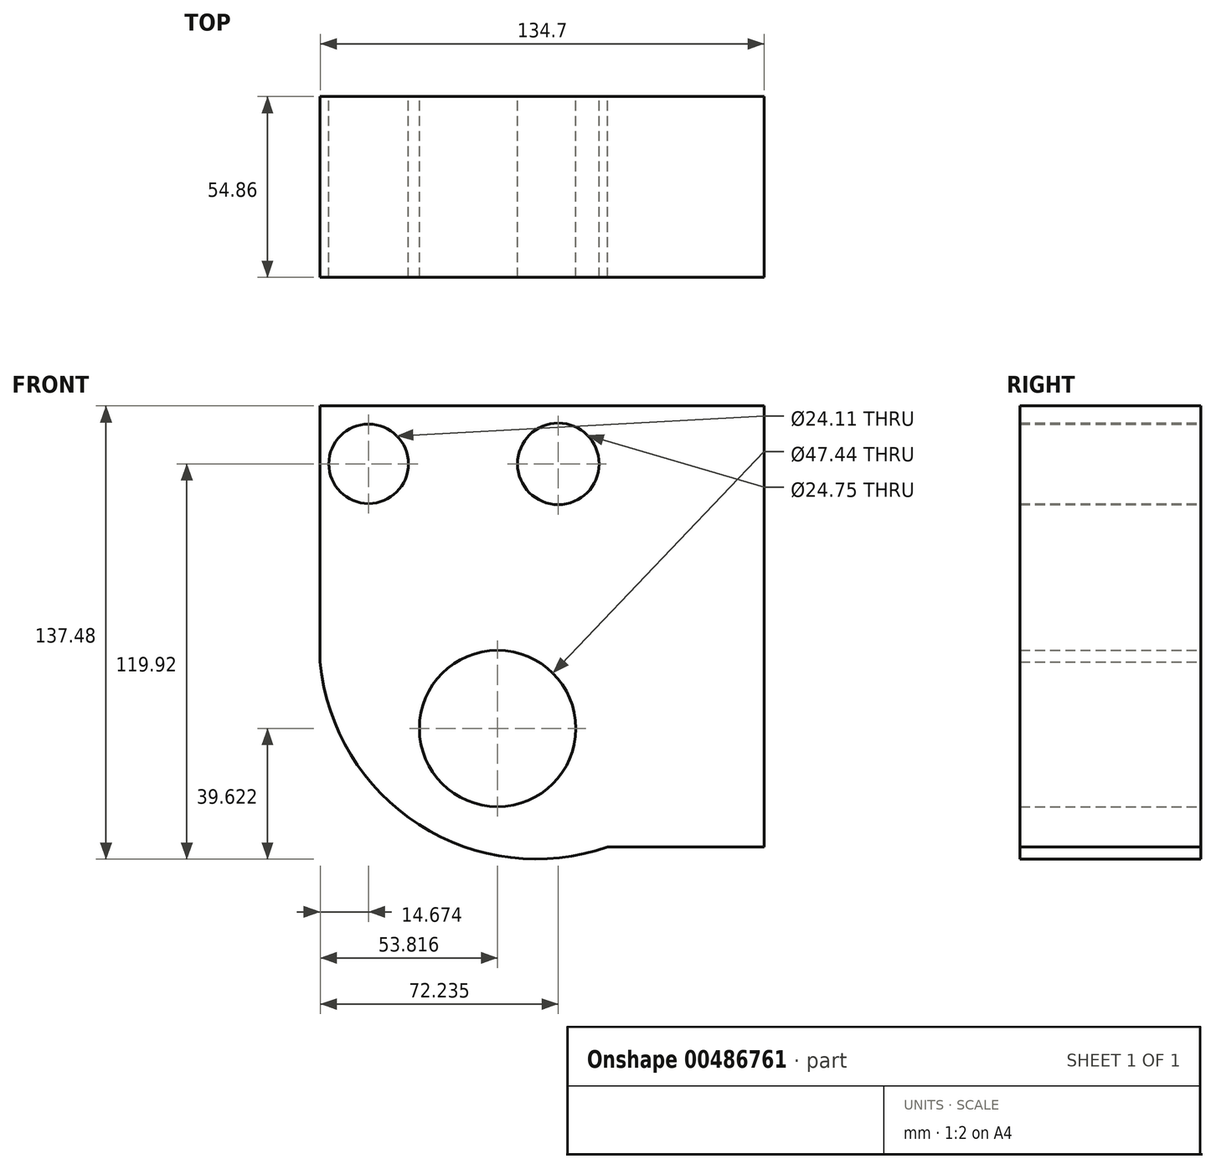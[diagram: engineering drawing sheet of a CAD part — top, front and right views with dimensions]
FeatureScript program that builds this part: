
annotation { "Feature Type Name" : "Feature", "Feature Type Description" : "" }
export const myFeature = defineFeature(function(context is Context, id is Id, definition is map)
    precondition{}
    {
        {
            var Q0;
            Q0=qCreatedBy(makeId("Front.planeOp"),FACE);
            var sketch = newSketch(context, id + "F0", { "sketchPlane" : qUnion([Q0])});
            skLineSegment(sketch, "E0", {"start": v(-42.24, 73.97) * mm, "end": v(44.96, 73.97) * mm});
            skLineSegment(sketch, "E1", {"start": v(44.96, 73.97) * mm, "end": v(44.96, -59.86) * mm});
            skLineSegment(sketch, "E2", {"start": v(-42.24, 73.97) * mm, "end": v(-42.24, -3.74) * mm});
            skArc(sketch, "E3", {"start": v(-42.24, -3.74) * mm, "mid": v(-12.3, -53.03) * mm, "end": v(44.96, -59.86) * mm});
            skCircle(sketch, "E4", {"center": v(11.58, -23.89) * mm, "radius": 23.72 * mm});
            skCircle(sketch, "E5", {"center": v(-27.57, 56.4) * mm, "radius": 12.05 * mm});
            skCircle(sketch, "E6", {"center": v(30, 56.4) * mm, "radius": 12.38 * mm});
            skSolve(sketch);
        }
        {
            var Q0;
            Q0 = qSketchRegion(id + "F0", true);
            extrude(context, id + "F1", {"entities" : qUnion([Q0]), "depth" : 54.86 * mm});
        }
        {
            var Q0;
            Q0=makeQuery(id+"F1.opExtrude","SWEPT_FACE",FACE,{"disambiguationData":[OSD([sQuery(id+"F0.wireOp",EDGE,"E1")])]});
            extrude(context, id + "F2", {"entities" : qUnion([Q0]), "operationType" : NewBodyOperationType.ADD, "depth" : 47.5 * mm});
        }
    });
